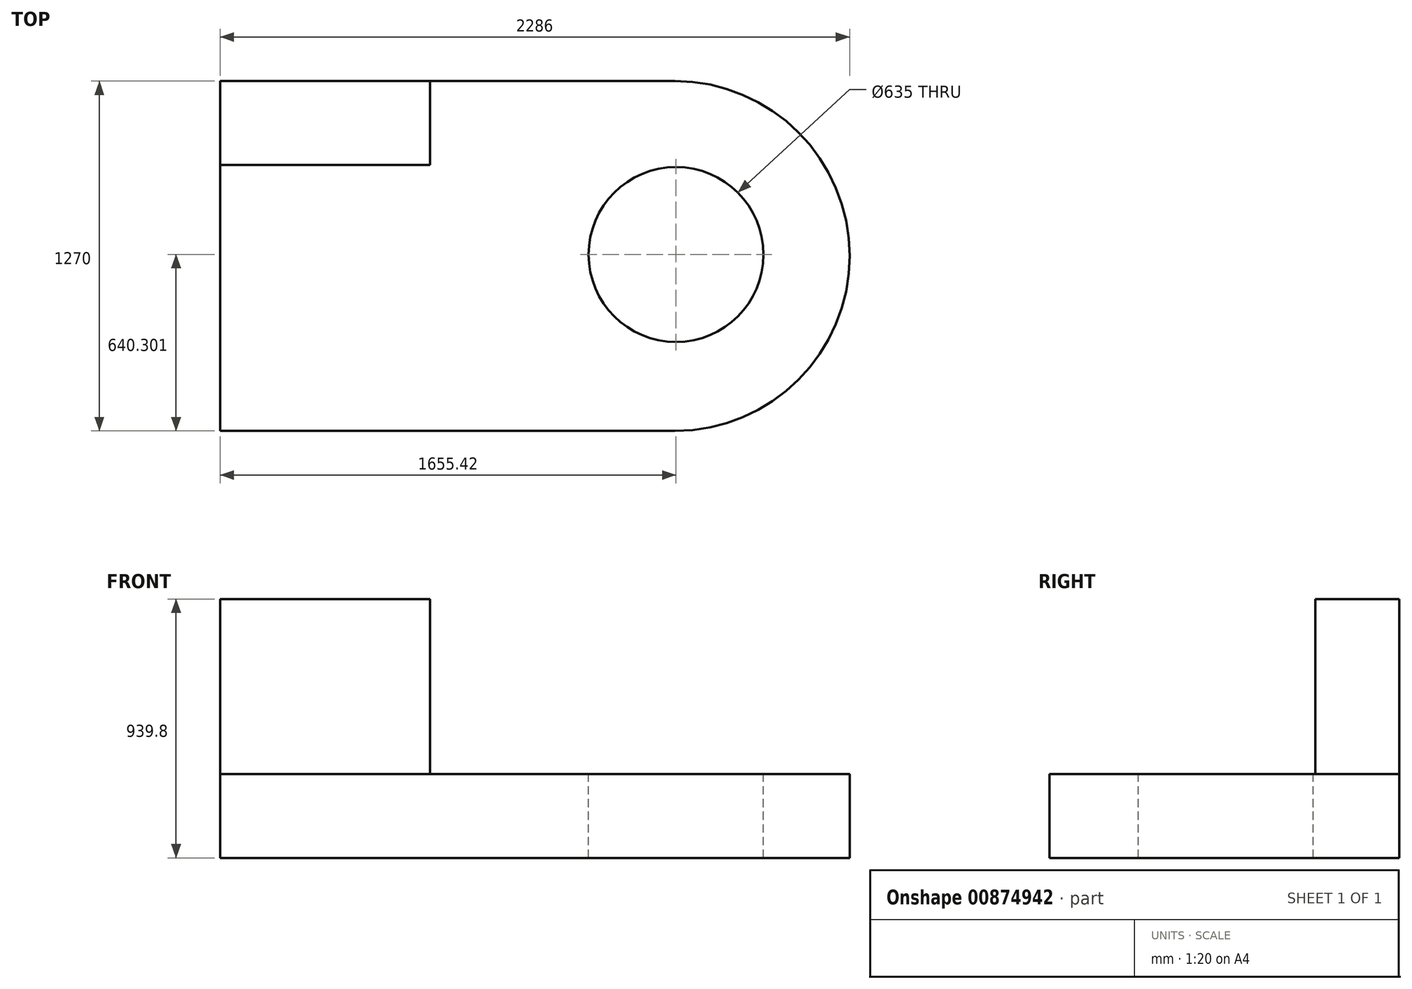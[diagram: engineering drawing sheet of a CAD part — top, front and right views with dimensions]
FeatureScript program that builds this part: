
annotation { "Feature Type Name" : "Feature", "Feature Type Description" : "" }
export const myFeature = defineFeature(function(context is Context, id is Id, definition is map)
    precondition{}
    {
        {
            var Q0;
            Q0=qCreatedBy(makeId("Front.planeOp"),FACE);
            var sketch = newSketch(context, id + "F0", { "sketchPlane" : qUnion([Q0])});
            skLineSegment(sketch, "E0.bottom", {"start": v(-153.83, -85.8) * mm, "end": v(1497.17, -85.8) * mm});
            skLineSegment(sketch, "E0.top", {"start": v(-153.83, 219) * mm, "end": v(1497.17, 219) * mm});
            skLineSegment(sketch, "E0.left", {"start": v(-153.83, -85.8) * mm, "end": v(-153.83, 219) * mm});
            skLineSegment(sketch, "E0.right", {"start": v(1497.17, -85.8) * mm, "end": v(1497.17, 219) * mm});
            skSolve(sketch);
        }
        {
            var Q0;
            Q0=makeQuery(id+"F0.imprint","IMPRINT",FACE,{"disambiguationData":[TD([[makeQuery(id+"F0.imprint","IMPRINT",EDGE,{"derivedFrom":sQuery(id+"F0.wireOp",EDGE,"E0.bottom")}),1.0]])]});
            extrude(context, id + "F1", {"entities" : qUnion([Q0]), "depth" : 1270 * mm, "offsetDistance" : 25.4 * mm});
        }
        {
            var Q0;
            Q0=makeQuery(id+"F1.opExtrude","SWEPT_FACE",FACE,{"disambiguationData":[OSD([sQuery(id+"F0.wireOp",EDGE,"E0.top")])]});
            var sketch = newSketch(context, id + "F2", { "sketchPlane" : qUnion([Q0])});
            skLineSegment(sketch, "E1.bottom", {"start": v(-153.83, 0) * mm, "end": v(608.17, 0) * mm});
            skLineSegment(sketch, "E1.top", {"start": v(-153.83, -304.8) * mm, "end": v(608.17, -304.8) * mm});
            skLineSegment(sketch, "E1.left", {"start": v(-153.83, 0) * mm, "end": v(-153.83, -304.8) * mm});
            skLineSegment(sketch, "E1.right", {"start": v(608.17, 0) * mm, "end": v(608.17, -304.8) * mm});
            skSolve(sketch);
        }
        {
            var Q0;
            Q0=makeQuery(id+"F2.imprint","IMPRINT",FACE,{"disambiguationData":[TD([[makeQuery(id+"F2.imprint","IMPRINT",EDGE,{"derivedFrom":sQuery(id+"F2.wireOp",EDGE,"E1.bottom")}),-1.0]])]});
            extrude(context, id + "F3", {"entities" : qUnion([Q0]), "operationType" : NewBodyOperationType.ADD, "depth" : 635 * mm, "offsetDistance" : 25.4 * mm});
        }
        {
            var Q0;
            Q0=makeQuery(id+"F1.opExtrude","SWEPT_FACE",FACE,{"disambiguationData":[OSD([sQuery(id+"F0.wireOp",EDGE,"E0.top")])]});
            var sketch = newSketch(context, id + "F4", { "sketchPlane" : qUnion([Q0])});
            skCircle(sketch, "E2", {"center": v(1497.17, -635) * mm, "radius": 635 * mm});
            skSolve(sketch);
        }
        {
            var Q0;
            {var subQ1=sQuery(id+"F0.wireOp",EDGE,"E0.top");var subQ2=makeQuery(id+"F1.opExtrude","SWEPT_EDGE",EDGE,{"disambiguationData":[OSD([subQ1,sQuery(id+"F0.wireOp",EDGE,"E0.right")])]});Q0=makeQuery(id+"F4.imprint","IMPRINT",FACE,{"disambiguationData":[TD([[makeQuery(id+"F4.imprint","IMPRINT",EDGE,{"derivedFrom":subQ2}),-1.0]])]});}
            extrude(context, id + "F5", {"entities" : qUnion([Q0]), "operationType" : NewBodyOperationType.ADD, "oppositeDirection" : true, "depth" : 304.8 * mm, "offsetDistance" : 25.4 * mm});
        }
        {
            var Q0;
            {var subQ0=sQuery(id+"F0.wireOp",EDGE,"E0.top");Q0=makeQuery(id+"F5.boolean.opBoolean","MERGE",FACE,{"derivedFrom":[makeQuery(id+"F1.opExtrude","SWEPT_FACE",FACE,{"disambiguationData":[OSD([subQ0])]}),makeQuery(id+"F5.opExtrude","CAP_FACE",FACE,{"disambiguationData":[OSD([subQ0,sQuery(id+"F0.wireOp",EDGE,"E0.right"),sQuery(id+"F4.wireOp",EDGE,"E2")])],"isStart":true})]});}
            var sketch = newSketch(context, id + "F6", { "sketchPlane" : qUnion([Q0])});
            skLineSegment(sketch, "E3", {"start": v(1497.17, -1270) * mm, "end": v(1497.17, -635) * mm});
            skSolve(sketch);
        }
        {
            var Q0;
            {var subQ0=sQuery(id+"F0.wireOp",EDGE,"E0.top");Q0=makeQuery(id+"F6.imprint","IMPRINT",FACE,{"disambiguationData":[TD([[makeQuery(id+"F6.imprint","IMPRINT",EDGE,{"derivedFrom":makeQuery(id+"F1.opExtrude","CAP_EDGE",EDGE,{"disambiguationData":[OSD([subQ0])],"isStart":false})}),1.0]])]});}
            var sketch = newSketch(context, id + "F7", { "sketchPlane" : qUnion([Q0])});
            skCircle(sketch, "E4", {"center": v(1501.6, -629.7) * mm, "radius": 317.5 * mm});
            skSolve(sketch);
        }
        {
            var Q0;
            Q0=makeQuery(id+"F7.imprint","IMPRINT",FACE,{"disambiguationData":[TD([[makeQuery(id+"F7.imprint","IMPRINT",EDGE,{"derivedFrom":sQuery(id+"F7.wireOp",EDGE,"E4")}),1.0]])]});
            extrude(context, id + "F8", {"entities" : qUnion([Q0]), "operationType" : NewBodyOperationType.REMOVE, "oppositeDirection" : true, "depth" : 576.58 * mm, "offsetDistance" : 25.4 * mm});
        }
    });
